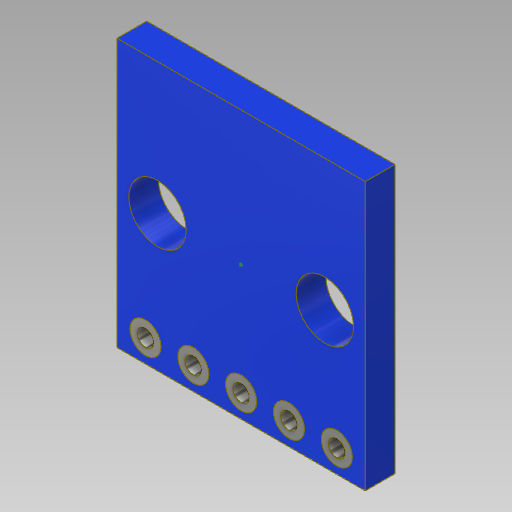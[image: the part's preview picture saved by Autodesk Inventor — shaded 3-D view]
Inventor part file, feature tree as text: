
AUTODESK INVENTOR PART (.ipt)
format: ipt  version: 2020 (Build 240168000, 168)  size: 179,712 bytes
history: native  units: in
note: dims shown in document units (in); Inventor stores cm internally (conversion verified against a paired STEP export)
features: sketch x5, extrude x4, mirror x1, projected_geometry x1
ambient origin geometry x8: Origin, YZ Plane, XZ Plane, XY Plane, X Axis, Y Axis, Z Axis, Center Point
bodies: Solid1 (feature_tree)
feature tree (11):
  extrude  "Extrusion1"  Depth=0.56in
  extrude  "Extrusion2"  Depth=0.062in
  extrude  "Extrusion3"  Depth=0.275in
  mirror  "Mirror1"
  extrude  "Extrusion4"  Depth=0.062in
  sketch  "Sketch5"  dims[d10=0.015in d11=0.2in d12=1.9685in d14=0.1in d15=0.3937in d17=1.0in d19=0.0001in d20=0.0in d21=0.035in d22=0.1in d23=1.9685in d25=0.1in d26=0.3937in d28=1.0in d30=0.0001in d31=0.0in]
  sketch  "Sketch1"  dims[d0=0.519in d1=0.56in]
  sketch  "Sketch2"  dims[d2=0.062in d3=0.0in d4=0.12in]
  sketch  "Sketch3"  dims[d5=0.35in d6=0.275in]
  sketch  "Sketch4"  dims[d7=0.062in d8=0.0in d9=0.065in]
  projected_geometry  "Projected Loop1"
